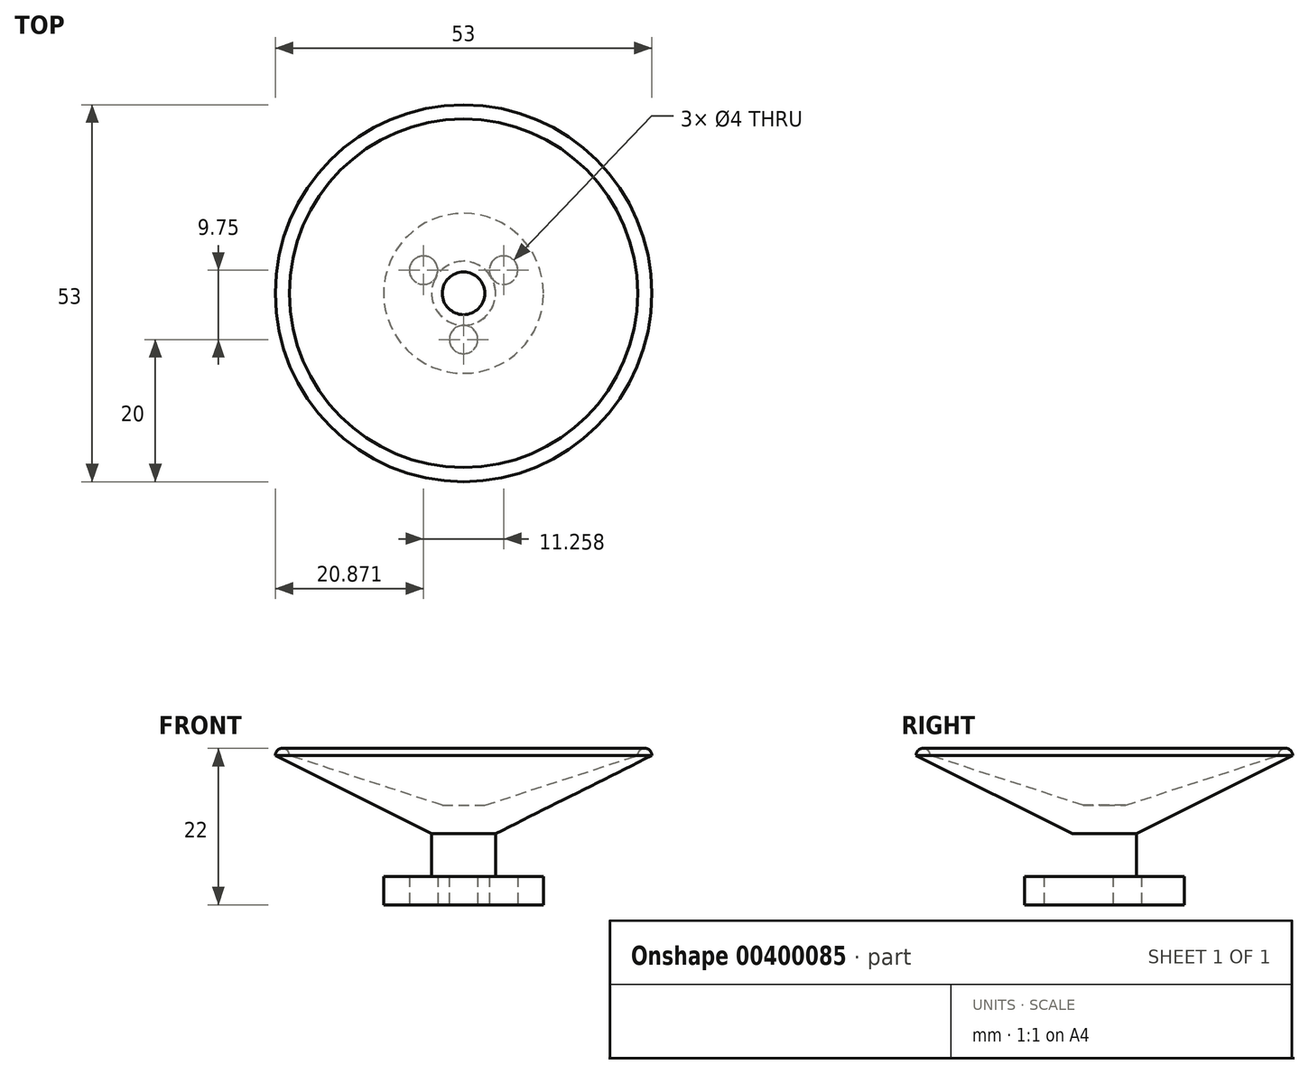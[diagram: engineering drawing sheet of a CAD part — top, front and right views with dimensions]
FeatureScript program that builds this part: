
annotation { "Feature Type Name" : "Feature", "Feature Type Description" : "" }
export const myFeature = defineFeature(function(context is Context, id is Id, definition is map)
    precondition{}
    {
        {
            var Q0;
            Q0=qCreatedBy(makeId("Top.planeOp"),FACE);
            var sketch = newSketch(context, id + "F0", { "sketchPlane" : qUnion([Q0])});
            skCircle(sketch, "E0", {"center": v(0, 0) * mm, "radius": 11.25 * mm});
            skSolve(sketch);
        }
        {
            var Q0;
            Q0 = qSketchRegion(id + "F0", true);
            extrude(context, id + "F1", {"entities" : qUnion([Q0]), "depth" : 4 * mm});
        }
        {
            var Q0;
            Q0=makeQuery(id+"F1.opExtrude","CAP_FACE",FACE,{"disambiguationData":[OSD([sQuery(id+"F0.wireOp",EDGE,"E0")])],"isStart":false});
            var sketch = newSketch(context, id + "F2", { "sketchPlane" : qUnion([Q0])});
            skCircle(sketch, "E1", {"center": v(0, 0) * mm, "radius": 4.5 * mm});
            skSolve(sketch);
        }
        {
            var Q0;
            Q0 = qSketchRegion(id + "F2", true);
            extrude(context, id + "F3", {"entities" : qUnion([Q0]), "operationType" : NewBodyOperationType.ADD, "depth" : 6 * mm});
        }
        {
            var Q0;
            Q0=qCreatedBy(makeId("Front.planeOp"),FACE);
            var sketch = newSketch(context, id + "F4", { "sketchPlane" : qUnion([Q0])});
            skLineSegment(sketch, "E2", {"start": v(0, 14) * mm, "end": v(3, 14) * mm});
            skLineSegment(sketch, "E3", {"start": v(3, 14) * mm, "end": v(24.5, 21) * mm});
            skLineSegment(sketch, "E4.0", {"start": v(0, 10) * mm, "end": v(4.5, 10) * mm});
            skLineSegment(sketch, "E5", {"start": v(4.5, 10) * mm, "end": v(26.5, 21) * mm});
            skLineSegment(sketch, "E6", {"start": v(0, 0) * mm, "end": v(0, 38.4) * mm, "construction": true});
            skLineSegment(sketch, "E7", {"start": v(24.5, 21) * mm, "end": v(26.5, 21) * mm, "construction": true});
            skArc(sketch, "E8", {"start": v(26.5, 21) * mm, "mid": v(25.5, 22) * mm, "end": v(24.5, 21) * mm});
            skLineSegment(sketch, "E9", {"start": v(21.34, 22) * mm, "end": v(29.98, 22) * mm, "construction": true});
            skLineSegment(sketch, "E10", {"start": v(0, 14) * mm, "end": v(0, 10) * mm});
            skSolve(sketch);
        }
        {
            var Q0;
            Q0 = qSketchRegion(id + "F4", true);
            var Q1;
            Q1=sQuery(id+"F4.wireOp",EDGE,"E6");
            revolve(context, id + "F5", {"operationType" : NewBodyOperationType.ADD, "entities" : qUnion([Q0]), "axis" : qUnion([Q1]), "revolveType" : RevolveType.FULL});
        }
        {
            var Q0;
            Q0=makeQuery(id+"F1.opExtrude","CAP_FACE",FACE,{"disambiguationData":[OSD([sQuery(id+"F0.wireOp",EDGE,"E0")])],"isStart":true});
            var sketch = newSketch(context, id + "F6", { "sketchPlane" : qUnion([Q0])});
            skCircle(sketch, "E11", {"center": v(0, 6.5) * mm, "radius": 2 * mm});
            skCircle(sketch, "E12.1.0", {"center": v(-5.63, -3.25) * mm, "radius": 2 * mm});
            skCircle(sketch, "E12.2.0", {"center": v(5.63, -3.25) * mm, "radius": 2 * mm});
            skPoint(sketch, "E12.center", {"position": v(0, 0) * mm});
            skSolve(sketch);
        }
        {
            var Q0;
            Q0=makeQuery(id+"F6.imprint","IMPRINT",FACE,{"disambiguationData":[TD([[makeQuery(id+"F6.imprint","IMPRINT",EDGE,{"derivedFrom":sQuery(id+"F6.wireOp",EDGE,"E12.1.0")}),1.0]])]});
            var Q1;
            Q1=makeQuery(id+"F6.imprint","IMPRINT",FACE,{"disambiguationData":[TD([[makeQuery(id+"F6.imprint","IMPRINT",EDGE,{"derivedFrom":sQuery(id+"F6.wireOp",EDGE,"E12.2.0")}),1.0]])]});
            var Q2;
            Q2=makeQuery(id+"F6.imprint","IMPRINT",FACE,{"disambiguationData":[TD([[makeQuery(id+"F6.imprint","IMPRINT",EDGE,{"derivedFrom":sQuery(id+"F6.wireOp",EDGE,"E11")}),1.0]])]});
            var Q3;
            Q3=makeQuery(id+"F1.opExtrude","CAP_FACE",FACE,{"disambiguationData":[OSD([sQuery(id+"F0.wireOp",EDGE,"E0")])],"isStart":false});
            extrude(context, id + "F7", {"entities" : qUnion([Q0, Q1, Q2]), "operationType" : NewBodyOperationType.REMOVE, "endBound" : BoundingType.UP_TO_SURFACE, "oppositeDirection" : true, "endBoundEntityFace" : qUnion([Q3]), "depth" : 25 * mm});
        }
    });
